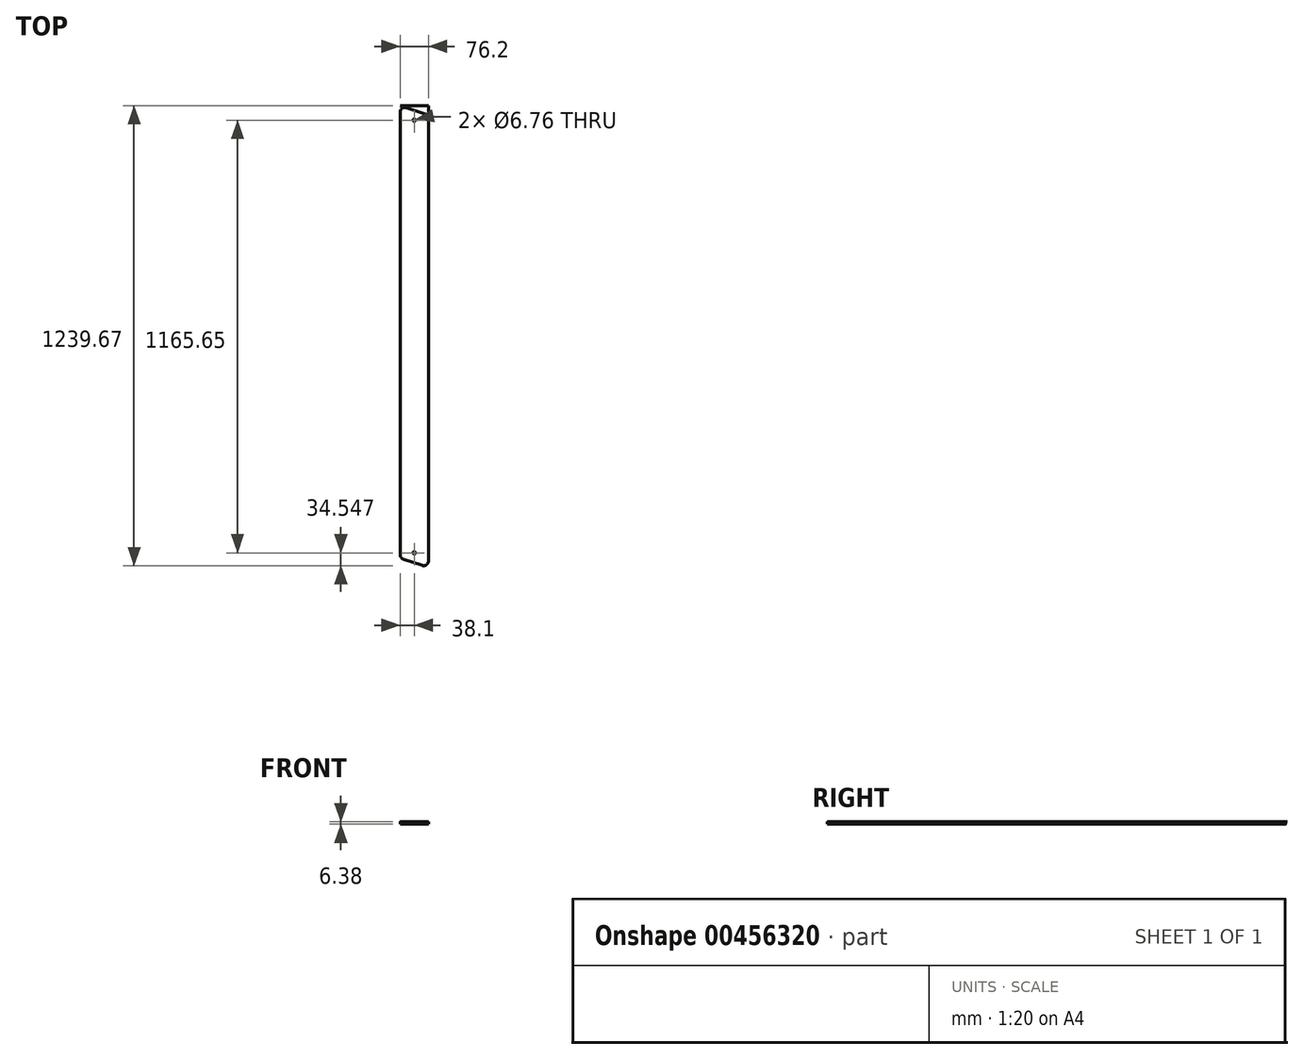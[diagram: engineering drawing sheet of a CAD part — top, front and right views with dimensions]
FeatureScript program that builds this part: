
annotation { "Feature Type Name" : "Feature", "Feature Type Description" : "" }
export const myFeature = defineFeature(function(context is Context, id is Id, definition is map)
    precondition{}
    {
        {
            var Q0;
            Q0=qCreatedBy(makeId("Top.planeOp"),FACE);
            var sketch = newSketch(context, id + "F0", { "sketchPlane" : qUnion([Q0])});
            skLineSegment(sketch, "E0", {"start": v(0, 635) * mm, "end": v(0, -635) * mm, "construction": true});
            skPoint(sketch, "E1", {"position": v(-38.1, 0) * mm});
            skPoint(sketch, "E2", {"position": v(-38.1, 609.6) * mm});
            skLineSegment(sketch, "E3", {"start": v(-38.1, 591.98) * mm, "end": v(-38.1, 0) * mm});
            skLineSegment(sketch, "E4", {"start": v(-21.38, 604.03) * mm, "end": v(29.42, 587.1) * mm});
            skPoint(sketch, "E5", {"position": v(38.1, -25.4) * mm});
            skLineSegment(sketch, "E6", {"start": v(38.1, 575.05) * mm, "end": v(38.1, -25.4) * mm});
            skPoint(sketch, "E7", {"position": v(-38.1, -609.6) * mm});
            skPoint(sketch, "E8", {"position": v(38.1, -635) * mm});
            skLineSegment(sketch, "E9", {"start": v(-38.1, 0) * mm, "end": v(-38.1, -600.45) * mm});
            skLineSegment(sketch, "E10", {"start": v(38.1, -25.4) * mm, "end": v(38.1, -617.37) * mm});
            skLineSegment(sketch, "E11", {"start": v(-29.42, -612.5) * mm, "end": v(21.38, -629.42) * mm});
            skPoint(sketch, "E12", {"position": v(38.1, 584.2) * mm});
            skArc(sketch, "E13.filletArc", {"start": v(-21.38, 604.03) * mm, "mid": v(-32.83, 602.28) * mm, "end": v(-38.1, 591.98) * mm});
            skArc(sketch, "E14.filletArc", {"start": v(38.1, 575.05) * mm, "mid": v(35.7, 582.48) * mm, "end": v(29.42, 587.1) * mm});
            skArc(sketch, "E15.filletArc", {"start": v(-38.1, -600.45) * mm, "mid": v(-35.7, -607.87) * mm, "end": v(-29.42, -612.5) * mm});
            skArc(sketch, "E16.filletArc", {"start": v(21.38, -629.42) * mm, "mid": v(32.83, -627.68) * mm, "end": v(38.1, -617.37) * mm});
            skLineSegment(sketch, "E17", {"start": v(-38.1, 609.6) * mm, "end": v(38.1, 584.2) * mm, "construction": true});
            skLineSegment(sketch, "E18", {"start": v(-38.1, 609.6) * mm, "end": v(-38.1, -609.6) * mm, "construction": true});
            skLineSegment(sketch, "E19", {"start": v(-38.1, -609.6) * mm, "end": v(38.1, -635) * mm, "construction": true});
            skLineSegment(sketch, "E20", {"start": v(38.1, -635) * mm, "end": v(38.1, 584.2) * mm, "construction": true});
            skPoint(sketch, "E21", {"position": v(0, 570.13) * mm});
            skPoint(sketch, "E22", {"position": v(0, -595.52) * mm});
            skPoint(sketch, "E23", {"position": v(0, 532.03) * mm});
            skPoint(sketch, "E24", {"position": v(-4.95, 532.03) * mm});
            skLineSegment(sketch, "E25", {"start": v(-4.95, 532.03) * mm, "end": v(0, 532.03) * mm});
            skPoint(sketch, "E26", {"position": v(-4.95, 0) * mm});
            skLineSegment(sketch, "E27", {"start": v(-4.95, 532.03) * mm, "end": v(-4.95, 0) * mm});
            skLineSegment(sketch, "E28.MirrorCS", {"start": v(4.95, 532.03) * mm, "end": v(0, 532.03) * mm});
            skLineSegment(sketch, "E29.MirrorCS", {"start": v(4.95, 532.03) * mm, "end": v(4.95, 0) * mm});
            skPoint(sketch, "E30", {"position": v(0, -557.42) * mm});
            skPoint(sketch, "E31", {"position": v(-4.95, -557.42) * mm});
            skLineSegment(sketch, "E32", {"start": v(-4.95, -557.42) * mm, "end": v(0, -557.42) * mm});
            skLineSegment(sketch, "E33", {"start": v(-4.95, 0) * mm, "end": v(-4.95, -557.42) * mm});
            skLineSegment(sketch, "E34.MirrorCS", {"start": v(4.95, 0) * mm, "end": v(4.95, -557.42) * mm});
            skLineSegment(sketch, "E35.MirrorCS", {"start": v(4.95, -557.42) * mm, "end": v(0, -557.42) * mm});
            skPoint(sketch, "E36", {"position": v(38.1, 609.6) * mm});
            skLineSegment(sketch, "E37", {"start": v(-38.1, 609.6) * mm, "end": v(38.1, 609.6) * mm});
            skLineSegment(sketch, "E38", {"start": v(38.1, 609.6) * mm, "end": v(38.1, 584.2) * mm});
            skLineSegment(sketch, "E39", {"start": v(-38.1, 609.6) * mm, "end": v(38.1, 584.2) * mm});
            skSolve(sketch);
        }
        {
            var Q0;
            Q0=makeQuery(id+"F0.imprint","IMPRINT",FACE,{"disambiguationData":[TD([[makeQuery(id+"F0.imprint","IMPRINT",EDGE,{"derivedFrom":sQuery(id+"F0.wireOp",EDGE,"E3")}),1.0]])]});
            var Q1;
            Q1=makeQuery(id+"F0.imprint","IMPRINT",FACE,{"disambiguationData":[TD([[makeQuery(id+"F0.imprint","IMPRINT",EDGE,{"derivedFrom":sQuery(id+"F0.wireOp",EDGE,"E25")}),-1.0]])]});
            extrude(context, id + "F1", {"entities" : qUnion([Q0, Q1]), "oppositeDirection" : true, "depth" : 6.35 * mm});
        }
        {
            var Q0;
            Q0=sQuery(id+"F0.wireOp",VERTEX,"E21");
            var Q1;
            Q1=sQuery(id+"F0.wireOp",VERTEX,"E22");
            var Q2;
            Q2=makeQuery(id+"F1.opExtrude","SWEPT_BODY",BODY,{"disambiguationData":[OSD([sQuery(id+"F0.wireOp",EDGE,"E3"),sQuery(id+"F0.wireOp",EDGE,"E4"),sQuery(id+"F0.wireOp",EDGE,"E6"),sQuery(id+"F0.wireOp",EDGE,"E9"),sQuery(id+"F0.wireOp",EDGE,"E10"),sQuery(id+"F0.wireOp",EDGE,"E11"),sQuery(id+"F0.wireOp",EDGE,"E13.filletArc"),sQuery(id+"F0.wireOp",EDGE,"E14.filletArc"),sQuery(id+"F0.wireOp",EDGE,"E15.filletArc"),sQuery(id+"F0.wireOp",EDGE,"E16.filletArc")])]});
            hole(context, id + "F2", {"style" : HoleStyle.SIMPLE, "endStyle" : HoleEndStyle.THROUGH, "standardTappedOrClearance" : lookupTablePath({ "standard" : "ANSI", "fit" : "Normal (ASME)", "size" : "1/4", "type" : "Clearance" }), "standardBlindInLast" : lookupTablePath({ "fit" : "Free", "standard" : "ANSI", "size" : "1/4", "type" : "Clearance" }), "holeDiameter" : 6.76 * mm, "locations" : qUnion([Q0, Q1]), "scope" : qUnion([Q2]), "isTappedThrough" : true});
        }
        {
            var Q0;
            {var subQ3=sQuery(id+"F0.wireOp",EDGE,"E37");Q0=makeQuery(id+"F0.imprint","IMPRINT",FACE,{"disambiguationData":[TD([[makeQuery(id+"F0.imprint","IMPRINT",EDGE,{"derivedFrom":subQ3}),-1.0]])]});}
            extrude(context, id + "F3", {"entities" : qUnion([Q0]), "depth" : 0.03 * mm});
        }
    });
